# Revit family: Exhaust_Fan-BroanNutone-Flex_DC-AE50110DC
name_source: partatom
category: Mechanical Equipment
units: mm (PartAtom-declared; Revit-internal decimal feet)

## family parameters
Classification = None
Cut with Voids When Loaded = No
Host = Face
OmniClass Number = 23.75.35.17.17
OmniClass Title = Room Air Circulation Fans
Part Type = Normal
Room Calculation Point = No
Round Connector Dimension = Use Radius
Shared = No

## types (1)
- AE50110DCL
    Assembly Code = E1090900
    Cover Finish = Plastic - Broan NuTone - White
    Default Elevation = 4' - 0"
    Description = Bathroom Exhaust Fan, ENERGY STAR®, 50-110 CFM
    Electrical Connector = Electrical Connection
    Exhaust Connector = Exhaust Connection
    Exhaust Diameter = 0' - 4"
    Exhaust Radius = 0' - 2"
    Frequency = 60 Hz
    Housing Height = 0' - 5 3/4"
    Housing Length = 0' - 10"
    Housing Width = 0' - 9 1/4"
    Length = 1' - 0 1/4"
    Manufacturer = Broan-NuTone
    Model = AE50110DCL
    Number of Poles = 1
    Phase = 1
    Power Factor = 1
    Product Documentation Link = https://www.broan-nutone.com
    Product Name = Broan® Bathroom Exhaust Fan, ENERGY STAR®, 50-110 CFM
    Product Page URL = https://www.broan-nutone.com
    URL = https://www.broan-nutone.com
    Version = 2019 v1.0a
    Voltage = 120 V
    Width = 0' - 11 1/2"

## geometry (parser evidence)
native form markers: Sweep x6
no freeform markers — native parametric forms only
